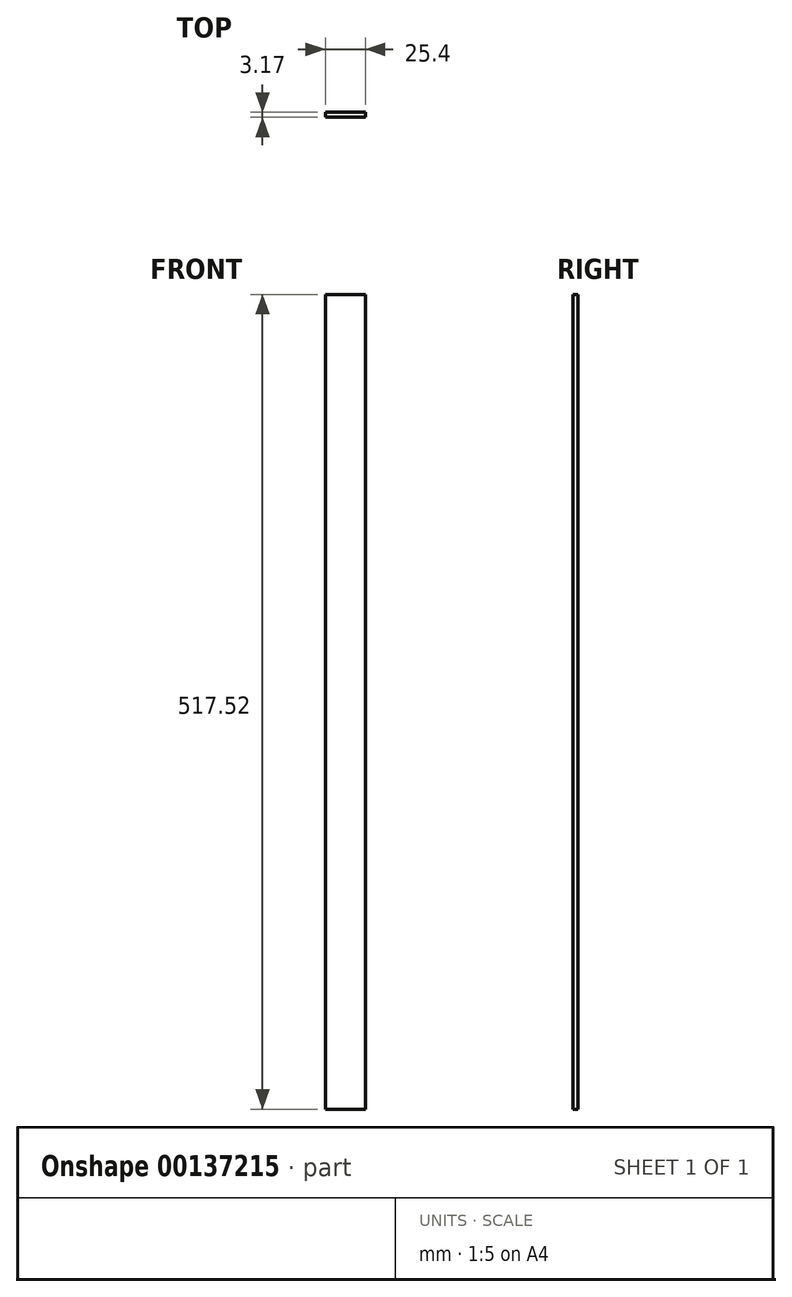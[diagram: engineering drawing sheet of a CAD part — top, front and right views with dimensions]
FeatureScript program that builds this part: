
annotation { "Feature Type Name" : "Feature", "Feature Type Description" : "" }
export const myFeature = defineFeature(function(context is Context, id is Id, definition is map)
    precondition{}
    {
        {
            var Q0;
            Q0=qCreatedBy(makeId("Top.planeOp"), FACE);
            var sketch = newSketch(context, id + "F0", { "sketchPlane" : qUnion([Q0])});
            skLineSegment(sketch, "E0.bottom", {"start": v(0, 0) * mm, "end": v(25.4, 0) * mm});
            skLineSegment(sketch, "E0.top", {"start": v(0, 3.18) * mm, "end": v(25.4, 3.18) * mm});
            skLineSegment(sketch, "E0.left", {"start": v(0, 0) * mm, "end": v(0, 3.17) * mm});
            skLineSegment(sketch, "E0.right", {"start": v(25.4, 0) * mm, "end": v(25.4, 3.17) * mm});
            skSolve(sketch);
        }
        {
            var Q0;
            Q0 = qSketchRegion(id + "F0", true);
            extrude(context, id + "F1", {"entities" : qUnion([Q0]), "depth" : 517.52 * mm, "offsetDistance" : 25.4 * mm});
        }
    });
